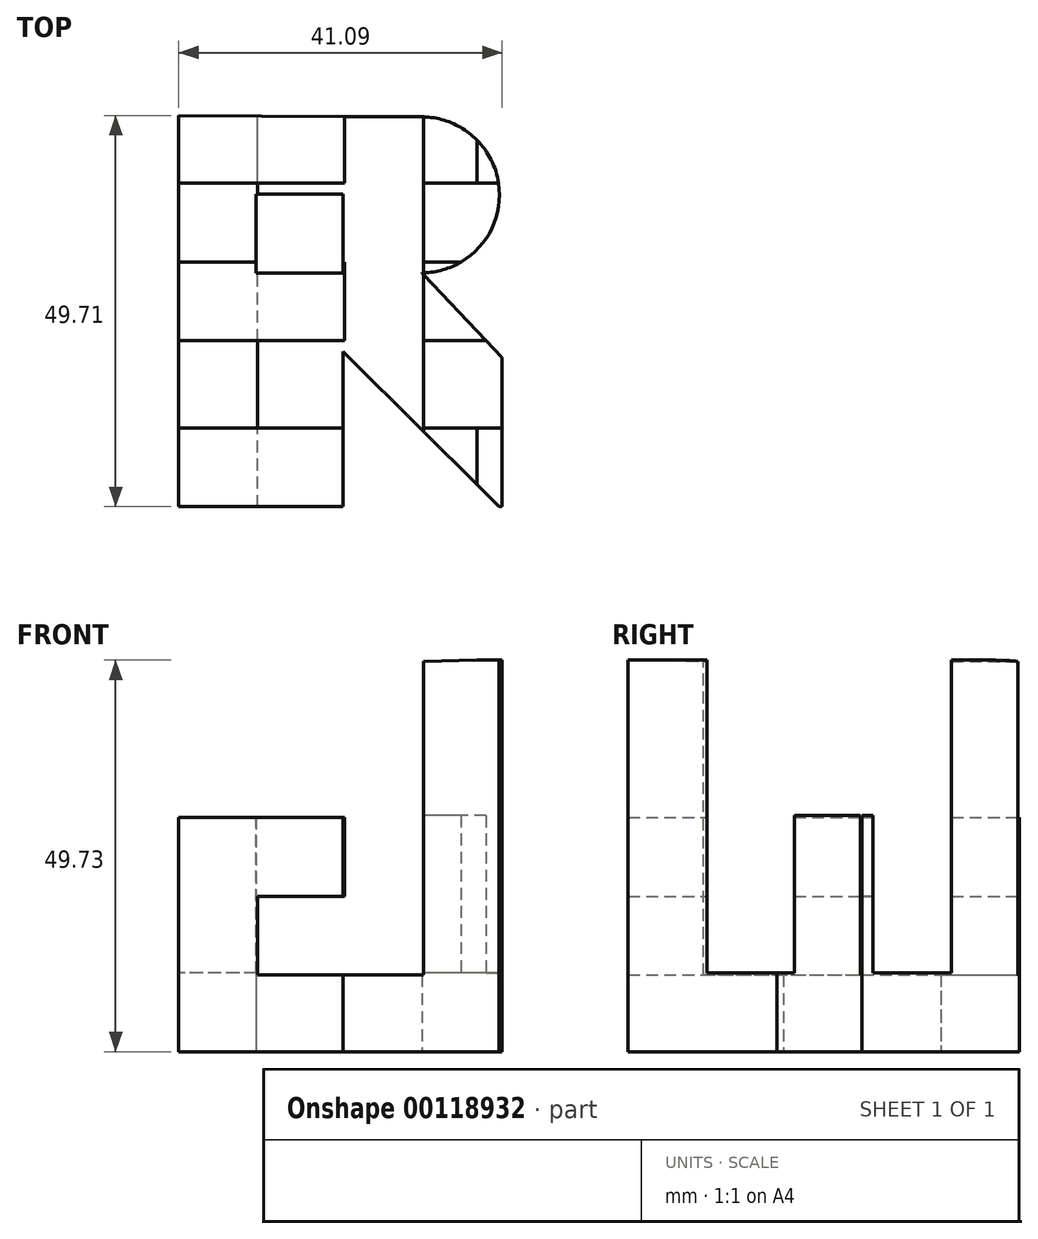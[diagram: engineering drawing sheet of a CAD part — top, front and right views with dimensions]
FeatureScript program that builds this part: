
annotation { "Feature Type Name" : "Feature", "Feature Type Description" : "" }
export const myFeature = defineFeature(function(context is Context, id is Id, definition is map)
    precondition{}
    {
        {
            var Q0;
            Q0=qCreatedBy(makeId("Front.planeOp"),FACE);
            var sketch = newSketch(context, id + "F0", { "sketchPlane" : qUnion([Q0])});
            skLineSegment(sketch, "E0.bottom", {"start": v(-25, -25) * mm, "end": v(25, -25) * mm, "construction": true});
            skLineSegment(sketch, "E0.left", {"start": v(-25, -25) * mm, "end": v(-25, 25) * mm, "construction": true});
            skLineSegment(sketch, "E0.right", {"start": v(25, -25) * mm, "end": v(25, 25) * mm, "construction": true});
            skPoint(sketch, "E0.middle", {"position": v(0, 0) * mm});
            skLineSegment(sketch, "E1", {"start": v(-15, 25) * mm, "end": v(-15, -25) * mm, "construction": true});
            skLineSegment(sketch, "E2", {"start": v(-3.91, 25) * mm, "end": v(-3.91, -25) * mm, "construction": true});
            skLineSegment(sketch, "E3", {"start": v(6.09, 24.82) * mm, "end": v(6.09, -25.18) * mm, "construction": true});
            skLineSegment(sketch, "E4", {"start": v(16.09, 25.09) * mm, "end": v(16.09, -24.91) * mm, "construction": true});
            skLineSegment(sketch, "E5", {"start": v(25, -10) * mm, "end": v(23.67, -9.19) * mm, "construction": true});
            skLineSegment(sketch, "E6", {"start": v(-25, -15) * mm, "end": v(25, -15) * mm, "construction": true});
            skLineSegment(sketch, "E7", {"start": v(25, -5) * mm, "end": v(-25, -5) * mm, "construction": true});
            skPoint(sketch, "E8.endSnap0", {"position": v(25, 0) * mm});
            skLineSegment(sketch, "E9", {"start": v(-25, -25) * mm, "end": v(16.09, -24.91) * mm});
            skLineSegment(sketch, "E10", {"start": v(16.09, -24.91) * mm, "end": v(16.09, 15) * mm});
            skLineSegment(sketch, "E11", {"start": v(6.09, 15) * mm, "end": v(6.09, -15) * mm});
            skLineSegment(sketch, "E12", {"start": v(6.09, -15) * mm, "end": v(-15, -15) * mm});
            skLineSegment(sketch, "E13", {"start": v(-15, -15) * mm, "end": v(-15, -5) * mm});
            skLineSegment(sketch, "E14", {"start": v(-15, -5) * mm, "end": v(-3.91, -5) * mm});
            skLineSegment(sketch, "E15", {"start": v(-3.91, -5) * mm, "end": v(-3.91, 5) * mm});
            skLineSegment(sketch, "E16", {"start": v(-3.91, 5) * mm, "end": v(-25, 5) * mm});
            skLineSegment(sketch, "E17", {"start": v(-25, 5) * mm, "end": v(-25, -5) * mm});
            skLineSegment(sketch, "E18", {"start": v(-25, -15) * mm, "end": v(-25, -25) * mm});
            skLineSegment(sketch, "E19", {"start": v(-25, -5) * mm, "end": v(-25, -15) * mm});
            skLineSegment(sketch, "E20", {"start": v(-25, 25) * mm, "end": v(-25, 15) * mm});
            skLineSegment(sketch, "E21", {"start": v(25, 15) * mm, "end": v(25, 25) * mm});
            skLineSegment(sketch, "E22", {"start": v(-15, 5) * mm, "end": v(-15, -5) * mm});
            skLineSegment(sketch, "E23", {"start": v(6.09, 24.82) * mm, "end": v(16.09, 25.09) * mm, "construction": true});
            skLineSegment(sketch, "E24", {"start": v(6.09, 24.82) * mm, "end": v(6.09, 15) * mm});
            skLineSegment(sketch, "E25", {"start": v(16.09, 25.09) * mm, "end": v(16.09, 15) * mm});
            skLineSegment(sketch, "E26", {"start": v(6.09, 24.82) * mm, "end": v(16.09, 25.09) * mm});
            skLineSegment(sketch, "E27", {"start": v(-25, 15) * mm, "end": v(25, 15) * mm, "construction": true});
            skLineSegment(sketch, "E28", {"start": v(-25, 25) * mm, "end": v(25, 25) * mm, "construction": true});
            skLineSegment(sketch, "E29", {"start": v(-3.91, 5) * mm, "end": v(25, 5) * mm, "construction": true});
            skSolve(sketch);
        }
        {
            var Q0;
            Q0=qCreatedBy(makeId("Right.planeOp"),FACE);
            var sketch = newSketch(context, id + "F1", { "sketchPlane" : qUnion([Q0])});
            skLineSegment(sketch, "E30.bottom", {"start": v(-24.82, -24.73) * mm, "end": v(25.18, -24.73) * mm, "construction": true});
            skLineSegment(sketch, "E30.top", {"start": v(-24.82, 25.27) * mm, "end": v(25.18, 25.27) * mm, "construction": true});
            skLineSegment(sketch, "E30.left", {"start": v(-24.82, -24.73) * mm, "end": v(-24.82, 25.27) * mm, "construction": true});
            skLineSegment(sketch, "E30.right", {"start": v(25.18, -24.73) * mm, "end": v(25.18, 25.27) * mm, "construction": true});
            skPoint(sketch, "E30.middle", {"position": v(0.18, 0.27) * mm});
            skLineSegment(sketch, "E31", {"start": v(-14.82, 25.27) * mm, "end": v(-14.82, -24.73) * mm, "construction": true});
            skLineSegment(sketch, "E32", {"start": v(-3.73, 25.27) * mm, "end": v(-3.73, -24.73) * mm, "construction": true});
            skLineSegment(sketch, "E33", {"start": v(6.27, 25.08) * mm, "end": v(6.27, -24.92) * mm, "construction": true});
            skLineSegment(sketch, "E34", {"start": v(16.27, 25.35) * mm, "end": v(16.27, -24.65) * mm, "construction": true});
            skLineSegment(sketch, "E35", {"start": v(-24.82, 15.27) * mm, "end": v(25.18, 15.27) * mm, "construction": true});
            skLineSegment(sketch, "E36", {"start": v(-24.82, -14.73) * mm, "end": v(25.18, -14.73) * mm, "construction": true});
            skLineSegment(sketch, "E37", {"start": v(25.18, -4.73) * mm, "end": v(-24.82, -4.73) * mm, "construction": true});
            skLineSegment(sketch, "E38", {"start": v(-24.82, 5.27) * mm, "end": v(25.18, 5.27) * mm, "construction": true});
            skPoint(sketch, "E38.endSnap0", {"position": v(25.18, 0.27) * mm});
            skLineSegment(sketch, "E39", {"start": v(-24.82, 25.27) * mm, "end": v(-24.82, -24.73) * mm});
            skLineSegment(sketch, "E40", {"start": v(25.18, -24.73) * mm, "end": v(-24.82, -24.73) * mm});
            skLineSegment(sketch, "E41", {"start": v(25.18, -24.73) * mm, "end": v(25.18, 25.27) * mm});
            skLineSegment(sketch, "E42", {"start": v(16.27, 25.35) * mm, "end": v(16.27, -14.73) * mm});
            skLineSegment(sketch, "E43", {"start": v(16.27, -14.73) * mm, "end": v(6.27, -14.73) * mm});
            skLineSegment(sketch, "E44", {"start": v(6.27, -14.73) * mm, "end": v(6.27, 3.4) * mm});
            skLineSegment(sketch, "E45", {"start": v(6.27, 3.4) * mm, "end": v(6.27, 5.27) * mm});
            skPoint(sketch, "E45.endSnap0", {"position": v(0.18, 5.27) * mm});
            skLineSegment(sketch, "E46", {"start": v(6.27, 5.27) * mm, "end": v(-3.73, 5.27) * mm});
            skLineSegment(sketch, "E47", {"start": v(-3.73, 5.27) * mm, "end": v(-3.73, -14.73) * mm});
            skLineSegment(sketch, "E48", {"start": v(-3.73, -14.73) * mm, "end": v(-14.82, -14.73) * mm});
            skLineSegment(sketch, "E49", {"start": v(-14.82, -14.73) * mm, "end": v(-14.82, 25.27) * mm});
            skLineSegment(sketch, "E50", {"start": v(-24.82, 25.27) * mm, "end": v(-14.82, 25.27) * mm});
            skLineSegment(sketch, "E51", {"start": v(16.27, 25.35) * mm, "end": v(25.18, 25.27) * mm});
            skSolve(sketch);
        }
        {
            var Q0;
            Q0=qCreatedBy(makeId("Top.planeOp"),FACE);
            var sketch = newSketch(context, id + "F2", { "sketchPlane" : qUnion([Q0])});
            skLineSegment(sketch, "E52.bottom", {"start": v(-25.2, -25.11) * mm, "end": v(24.8, -25.11) * mm, "construction": true});
            skLineSegment(sketch, "E52.top", {"start": v(-25.2, 24.89) * mm, "end": v(24.8, 24.89) * mm, "construction": true});
            skLineSegment(sketch, "E52.left", {"start": v(-25.2, -25.11) * mm, "end": v(-25.2, 24.89) * mm, "construction": true});
            skLineSegment(sketch, "E52.right", {"start": v(24.8, -25.11) * mm, "end": v(24.8, 24.89) * mm, "construction": true});
            skPoint(sketch, "E52.middle", {"position": v(-0.2, -0.11) * mm});
            skLineSegment(sketch, "E53", {"start": v(-15.2, 24.89) * mm, "end": v(-15.2, -25.11) * mm, "construction": true});
            skLineSegment(sketch, "E54", {"start": v(5.9, 24.7) * mm, "end": v(5.9, -25.3) * mm, "construction": true});
            skLineSegment(sketch, "E55", {"start": v(15.9, 24.98) * mm, "end": v(15.9, -25.02) * mm, "construction": true});
            skLineSegment(sketch, "E56", {"start": v(-25.2, 14.89) * mm, "end": v(-13.35, 14.89) * mm, "construction": true});
            skLineSegment(sketch, "E57", {"start": v(-25.2, -15.11) * mm, "end": v(24.8, -15.11) * mm, "construction": true});
            skLineSegment(sketch, "E58", {"start": v(24.8, -5.11) * mm, "end": v(-25.2, -5.11) * mm, "construction": true});
            skLineSegment(sketch, "E59", {"start": v(-25.2, 4.89) * mm, "end": v(24.8, 4.89) * mm, "construction": true});
            skPoint(sketch, "E59.endSnap0", {"position": v(24.8, -0.11) * mm});
            skLineSegment(sketch, "E60", {"start": v(-25.2, 24.89) * mm, "end": v(-25.2, -25.11) * mm});
            skLineSegment(sketch, "E61", {"start": v(-25.2, 24.89) * mm, "end": v(5.9, 24.7) * mm});
            skLineSegment(sketch, "E62", {"start": v(-25.2, -25.11) * mm, "end": v(-4.1, -25.11) * mm});
            skLineSegment(sketch, "E63", {"start": v(-4.1, -25.11) * mm, "end": v(-4.1, -5.11) * mm});
            skLineSegment(sketch, "E64", {"start": v(-4.1, -5.11) * mm, "end": v(15.9, -25.02) * mm});
            skLineSegment(sketch, "E65", {"start": v(15.9, -25.02) * mm, "end": v(24.8, -25.11) * mm});
            skLineSegment(sketch, "E66", {"start": v(5.9, 4.89) * mm, "end": v(24.8, -15.11) * mm});
            skLineSegment(sketch, "E67", {"start": v(24.8, -15.11) * mm, "end": v(24.8, -25.11) * mm});
            skArc(sketch, "E68", {"start": v(5.9, 4.89) * mm, "mid": v(15.74, 14.8) * mm, "end": v(5.9, 24.7) * mm});
            skLineSegment(sketch, "E69", {"start": v(-15.2, 14.89) * mm, "end": v(-4.1, 14.89) * mm, "construction": true});
            skLineSegment(sketch, "E70", {"start": v(-4.1, 4.89) * mm, "end": v(-15.2, 4.89) * mm, "construction": true});
            skLineSegment(sketch, "E71", {"start": v(-15.2, 4.89) * mm, "end": v(-15.2, 14.89) * mm, "construction": true});
            skLineSegment(sketch, "E72", {"start": v(-15.2, 14.89) * mm, "end": v(-4.1, 14.89) * mm});
            skLineSegment(sketch, "E73", {"start": v(-4.1, 4.89) * mm, "end": v(-15.2, 4.89) * mm});
            skLineSegment(sketch, "E74", {"start": v(-15.2, 14.89) * mm, "end": v(-15.2, 4.89) * mm});
            skLineSegment(sketch, "E75", {"start": v(-4.1, 4.89) * mm, "end": v(-4.1, 14.89) * mm});
            skLineSegment(sketch, "E76.trimOffspring", {"start": v(-4.1, 14.89) * mm, "end": v(24.8, 14.89) * mm, "construction": true});
            skSolve(sketch);
        }
        {
            var Q0;
            Q0 = qSketchRegion(id + "F0", true);
            extrude(context, id + "F3", {"entities" : qUnion([Q0]), "endBound" : BoundingType.SYMMETRIC, "depth" : 50 * mm});
        }
        {
            var Q0;
            Q0 = qSketchRegion(id + "F1", true);
            extrude(context, id + "F4", {"entities" : qUnion([Q0]), "operationType" : NewBodyOperationType.INTERSECT, "endBound" : BoundingType.SYMMETRIC, "depth" : 50 * mm});
        }
        {
            var Q0;
            Q0 = qSketchRegion(id + "F2", true);
            extrude(context, id + "F5", {"entities" : qUnion([Q0]), "operationType" : NewBodyOperationType.INTERSECT, "endBound" : BoundingType.SYMMETRIC, "depth" : 50 * mm});
        }
    });
